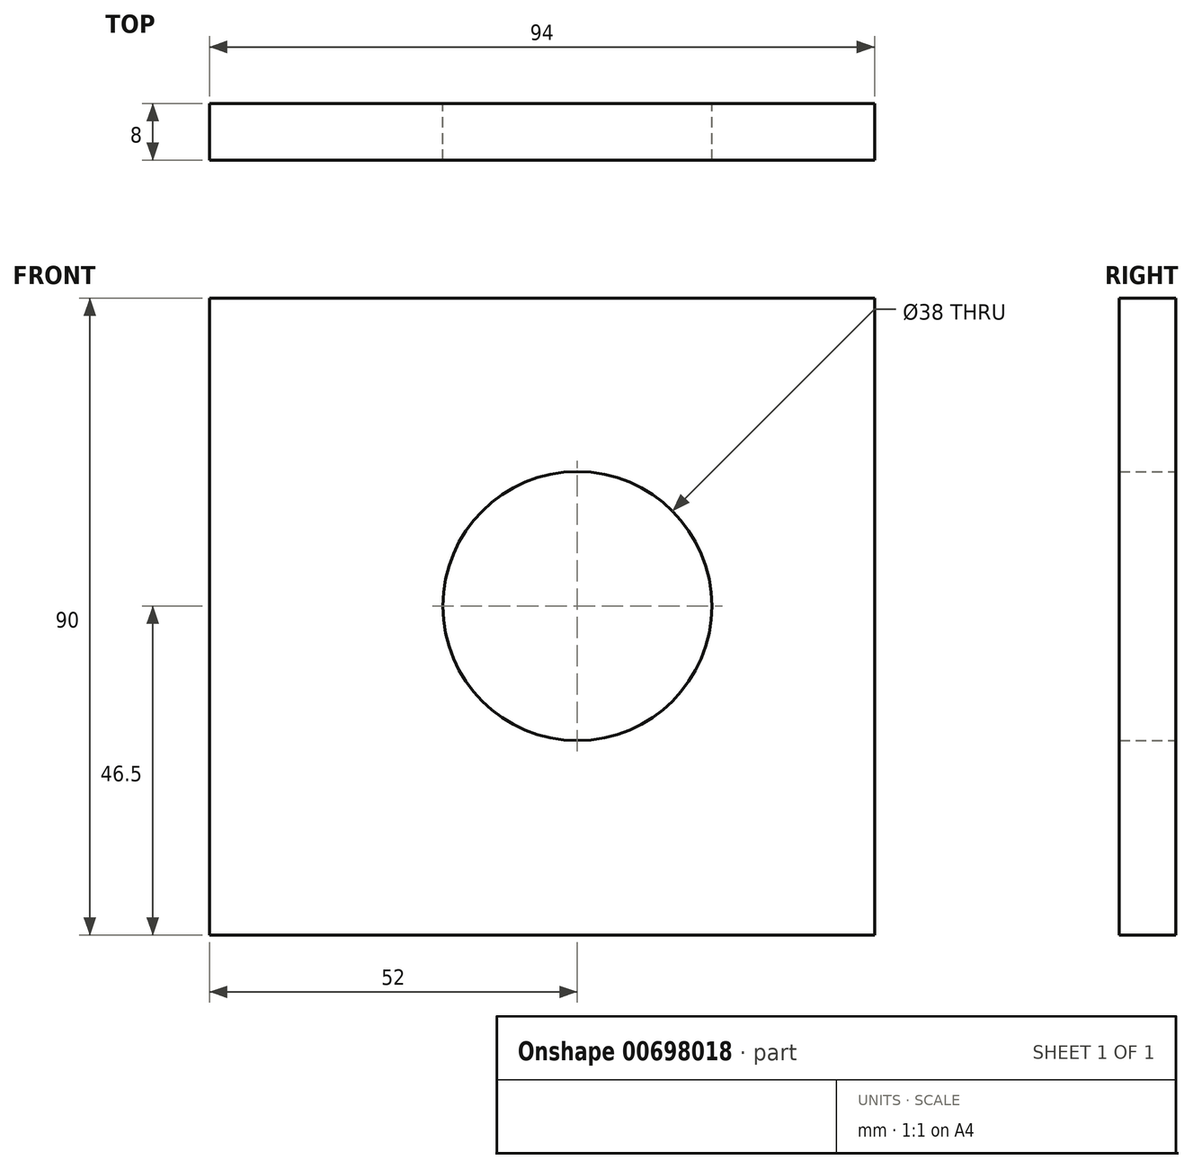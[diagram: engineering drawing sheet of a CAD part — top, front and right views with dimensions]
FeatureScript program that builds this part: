
annotation { "Feature Type Name" : "Feature", "Feature Type Description" : "" }
export const myFeature = defineFeature(function(context is Context, id is Id, definition is map)
    precondition{}
    {
        {
            var Q0;
            Q0=qCreatedBy(makeId("Front.planeOp"),FACE);
            var sketch = newSketch(context, id + "F0", { "sketchPlane" : qUnion([Q0])});
            skLineSegment(sketch, "E0", {"start": v(0, 0) * mm, "end": v(0, 90) * mm});
            skLineSegment(sketch, "E1", {"start": v(0, 90) * mm, "end": v(94, 90) * mm});
            skLineSegment(sketch, "E2", {"start": v(94, 90) * mm, "end": v(94, 0) * mm});
            skLineSegment(sketch, "E3", {"start": v(94, 0) * mm, "end": v(0, 0) * mm});
            skCircle(sketch, "E4", {"center": v(52, 46.5) * mm, "radius": 19 * mm});
            skSolve(sketch);
        }
        {
            var Q0;
            Q0=makeQuery(id+"F0.imprint","IMPRINT",FACE,{"disambiguationData":[TD([[makeQuery(id+"F0.imprint","IMPRINT",EDGE,{"derivedFrom":sQuery(id+"F0.wireOp",EDGE,"E0")}),-1.0]])]});
            extrude(context, id + "F1", {"entities" : qUnion([Q0]), "depth" : 8 * mm, "offsetDistance" : 25 * mm});
        }
    });
